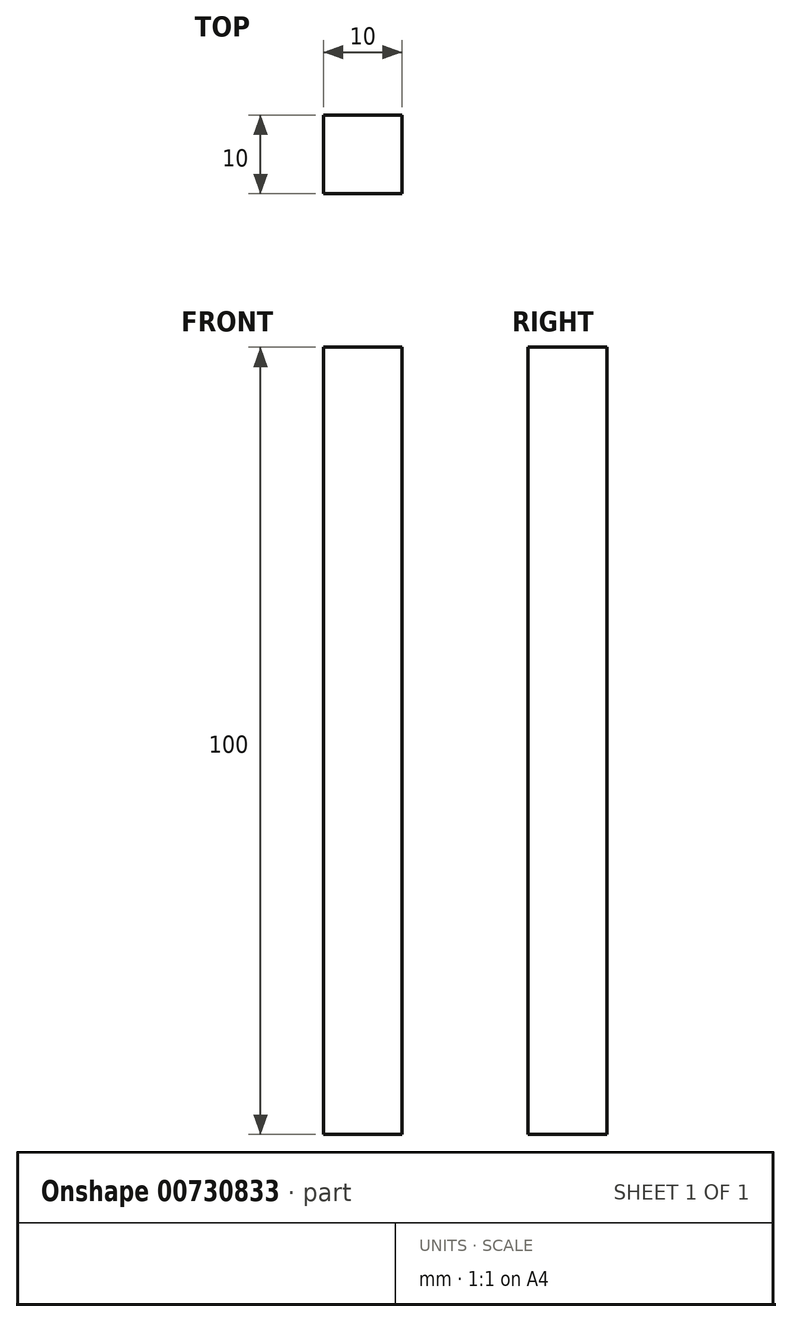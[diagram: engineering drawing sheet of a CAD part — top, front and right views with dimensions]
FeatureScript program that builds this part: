
annotation { "Feature Type Name" : "Feature", "Feature Type Description" : "" }
export const myFeature = defineFeature(function(context is Context, id is Id, definition is map)
    precondition{}
    {
        {
            var Q0;
            Q0=qCreatedBy(makeId("Top.planeOp"),FACE);
            var sketch = newSketch(context, id + "F0", { "sketchPlane" : qUnion([Q0])});
            skLineSegment(sketch, "E0.bottom", {"start": v(-4.46, 4.36) * mm, "end": v(5.54, 4.36) * mm});
            skLineSegment(sketch, "E0.top", {"start": v(-4.46, -5.64) * mm, "end": v(5.54, -5.64) * mm});
            skLineSegment(sketch, "E0.left", {"start": v(-4.46, 4.36) * mm, "end": v(-4.46, -5.64) * mm});
            skLineSegment(sketch, "E0.right", {"start": v(5.54, 4.36) * mm, "end": v(5.54, -5.64) * mm});
            skSolve(sketch);
        }
        {
            var Q0;
            Q0 = qSketchRegion(id + "F0", true);
            extrude(context, id + "F1", {"entities" : qUnion([Q0]), "depth" : 100 * mm, "offsetDistance" : 25.4 * mm});
        }
    });
